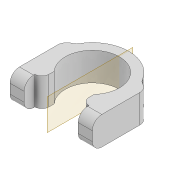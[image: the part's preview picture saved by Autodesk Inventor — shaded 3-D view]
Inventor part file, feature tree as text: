
AUTODESK INVENTOR PART (.ipt)
format: ipt  version: 2022 (Build 260153000, 153)  size: 168,448 bytes
history: native  units: mm
features: fillet x3, extrude x2, sketch x2, projected_geometry x2, mirror x1
ambient origin geometry x8: Origin, YZ Plane, XZ Plane, XY Plane, X Axis, Y Axis, Z Axis, Center Point
bodies: Solid1 (feature_tree)
feature tree (10):
  extrude  "Extrusion1"  Depth=2.0mm
  fillet  "Fillet1"  Radius=1.0mm
  extrude  "Extrusion3"  Depth=1.5mm
  fillet  "Fillet2"  Radius=6.0mm
  mirror  "Mirror1"
  fillet  "Fillet5"  Radius=1.5mm
  sketch  "Sketch1"  dims[d0=11.5mm d1=2.0mm d3=1.0mm]
  sketch  "Sketch4"  dims[d4=1.5mm d5=1.5mm d6=6.0mm d7=0.0mm d8=1.5mm d14=2.0mm d15=0.0mm d16=2.0mm d22=3.0mm d29=2.0mm d28=0.5mm d30=0.5mm d31=0.872665mm d32=0.0mm]
  projected_geometry  "Projected Loop2"
  projected_geometry  "Projected Loop4"
